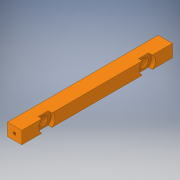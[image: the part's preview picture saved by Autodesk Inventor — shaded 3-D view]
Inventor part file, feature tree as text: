
AUTODESK INVENTOR PART (.ipt)
format: ipt  version: 2019 (Build 230136000, 136)  size: 138,752 bytes
history: native  units: in
note: dims shown in document units (in); Inventor stores cm internally (conversion verified against a paired STEP export)
features: sketch x4, extrude x2, hole x2, other x1, mirror x1, projected_geometry x1
ambient origin geometry x8: Origin, YZ Plane, XZ Plane, XY Plane, X Axis, Y Axis, Z Axis, Center Point
bodies: Solid1 (feature_tree)
feature tree (11):
  extrude  "Extrusion1"  Depth=0.565in
  extrude  "Extrusion2"  Depth=0.5in
  hole  "Hole1"  [1 undecoded]
  hole  "Hole2"  [1 undecoded]
  other  "MidPlane"
  mirror  "Mirror2"
  sketch  "Sketch1"  dims[d0=6.0in d1=0.565in]
  sketch  "Sketch2"  dims[d2=0.5in d3=0.0in d4=0.375in]
  sketch  "Sketch4"  dims[d5=0.375in d6=4.0in]
  sketch  "Sketch5"  dims[d7=6.0in d8=1.0in d9=0.5in d10=0.25in d11=0.25in d12=0.5in d13=0.0in d43=0.64in d44=0.75in d45=0.375in d46=0.25in d47=0.5635in d48=0.15in d49=0.0in d50=0.565in d51=0.5in d52=0.25in d53=0.2825in d54=0.104in d55=0.5in d56=0.375in d57=0.25in d58=0.5635in d59=0.5in d60=0.0in]
  projected_geometry  "Projected Loop1"
note: 2 required parameter values undecoded (feature->parameter linkage not recoverable at this tier; creation-order binding heuristic only, values carry confidence <= 0.55)
